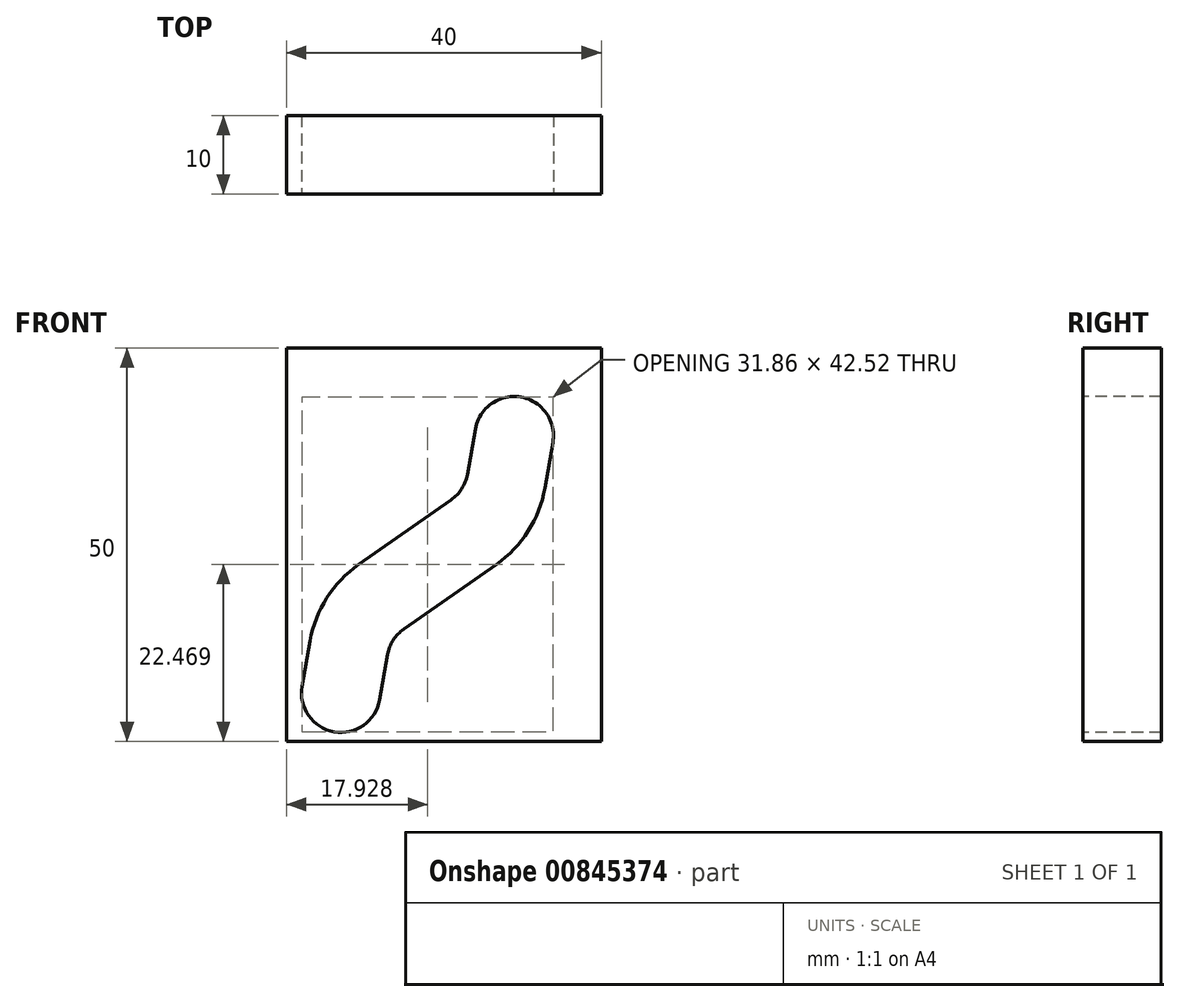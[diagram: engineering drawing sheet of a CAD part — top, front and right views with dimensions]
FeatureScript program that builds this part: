
annotation { "Feature Type Name" : "Feature", "Feature Type Description" : "" }
export const myFeature = defineFeature(function(context is Context, id is Id, definition is map)
    precondition{}
    {
        {
            var Q0;
            Q0=qCreatedBy(makeId("Front.planeOp"),FACE);
            var sketch = newSketch(context, id + "F0", { "sketchPlane" : qUnion([Q0])});
            skLineSegment(sketch, "E0.bottom", {"start": v(0, 0) * mm, "end": v(40, 0) * mm});
            skLineSegment(sketch, "E0.top", {"start": v(0, 50) * mm, "end": v(40, 50) * mm});
            skLineSegment(sketch, "E0.left", {"start": v(0, 0) * mm, "end": v(0, 50) * mm});
            skLineSegment(sketch, "E0.right", {"start": v(40, 0) * mm, "end": v(40, 50) * mm});
            skSolve(sketch);
        }
        {
            var Q0;
            Q0 = qSketchRegion(id + "F0", true);
            extrude(context, id + "F1", {"entities" : qUnion([Q0]), "depth" : 10 * mm, "offsetDistance" : 25 * mm});
        }
        {
            var Q0;
            Q0=makeQuery(id+"F1.opExtrude","CAP_FACE",FACE,{"disambiguationData":[OSD([sQuery(id+"F0.wireOp",EDGE,"E0.bottom"),sQuery(id+"F0.wireOp",EDGE,"E0.top"),sQuery(id+"F0.wireOp",EDGE,"E0.left"),sQuery(id+"F0.wireOp",EDGE,"E0.right")])],"isStart":false});
            var sketch = newSketch(context, id + "F2", { "sketchPlane" : qUnion([Q0])});
            skArc(sketch, "E1", {"start": v(2, 7) * mm, "mid": v(6.06, 1.2) * mm, "end": v(11.85, 5.26) * mm});
            skArc(sketch, "E2", {"start": v(33.86, 37.94) * mm, "mid": v(29.8, 43.73) * mm, "end": v(24, 39.67) * mm});
            skLineSegment(sketch, "E3", {"start": v(6.92, 6.13) * mm, "end": v(8.66, 15.98) * mm, "construction": true});
            skLineSegment(sketch, "E4", {"start": v(28.93, 38.8) * mm, "end": v(27.2, 28.96) * mm, "construction": true});
            skLineSegment(sketch, "E5", {"start": v(8.66, 15.98) * mm, "end": v(27.2, 28.96) * mm, "construction": true});
            skLineSegment(sketch, "E6.0", {"start": v(24, 39.67) * mm, "end": v(23, 33.9) * mm});
            skLineSegment(sketch, "E7.0", {"start": v(33.86, 37.94) * mm, "end": v(32.84, 32.17) * mm});
            skLineSegment(sketch, "E8.0", {"start": v(2, 7) * mm, "end": v(3.02, 12.77) * mm});
            skLineSegment(sketch, "E9.0", {"start": v(11.85, 5.26) * mm, "end": v(12.87, 11.03) * mm});
            skLineSegment(sketch, "E10.0", {"start": v(14.92, 14.26) * mm, "end": v(26.67, 22.49) * mm});
            skLineSegment(sketch, "E11.0", {"start": v(9.19, 22.45) * mm, "end": v(20.93, 30.68) * mm});
            skArc(sketch, "E12.filletArc", {"start": v(20.93, 30.68) * mm, "mid": v(22.28, 32.09) * mm, "end": v(23, 33.9) * mm});
            skArc(sketch, "E13.filletArc", {"start": v(14.92, 14.26) * mm, "mid": v(13.57, 12.85) * mm, "end": v(12.87, 11.03) * mm});
            skArc(sketch, "E14.filletArc", {"start": v(9.19, 22.45) * mm, "mid": v(5.14, 18.22) * mm, "end": v(3.02, 12.77) * mm});
            skArc(sketch, "E15.filletArc", {"start": v(26.67, 22.49) * mm, "mid": v(30.72, 26.71) * mm, "end": v(32.84, 32.17) * mm});
            skLineSegment(sketch, "E16.0", {"start": v(6.92, 6.13) * mm, "end": v(22.68, 3.35) * mm, "construction": true});
            skLineSegment(sketch, "E16.1", {"start": v(22.68, 3.35) * mm, "end": v(28.93, 38.8) * mm, "construction": true});
            skLineSegment(sketch, "E16.9", {"start": v(6.92, 6.13) * mm, "end": v(6.92, 6.13) * mm});
            skSolve(sketch);
        }
        {
            var Q0;
            Q0 = qSketchRegion(id + "F2", true);
            extrude(context, id + "F3", {"entities" : qUnion([Q0]), "operationType" : NewBodyOperationType.REMOVE, "endBound" : BoundingType.THROUGH_ALL, "oppositeDirection" : true, "depth" : 25 * mm, "offsetDistance" : 25 * mm});
        }
    });
